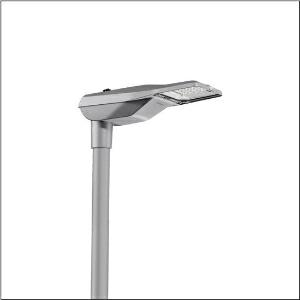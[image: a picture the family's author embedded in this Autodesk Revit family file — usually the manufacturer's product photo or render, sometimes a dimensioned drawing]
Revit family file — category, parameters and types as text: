
# Revit family: streetlight_sl_21_micro___st1_5a_5xe1p43s08db_ce40
name_source: partatom
category: Lighting Fixtures
units: mm (PartAtom-declared; Revit-internal decimal feet)

## family parameters
Cut with Voids When Loaded = No
Host = Face
Light Source = No
Part Type = Normal
Room Calculation Point = No
Round Connector Dimension = Use Diameter
Shared = No

## types (1)
- --- (1 x LED, 5230 lm, 39.1 W, 4000K)
    Apparent Load = 39 VA
    CIE Flux Codes = 22 53 95 100 100
    Color Rendering = 70
    Color Temperature = 4000K
    Default Elevation = 1800 mm
    Description = Streetlight SL 21 micro, mast luminaire, primary light control with lens, of PMMA, primary optical cover: cover, of toughened safety glass, transparent, light distribution: ST1.5a, light emission: direct distribution, primary light characteristic: asymmetric, installation type: side-entry, post-top, LED, High Power LED, rated luminous flux: 5.230lm, luminous efficacy: 134lm/W, light colour: 740, colour temperature: 4000K, control: flexible luminous flux parameterisation, time-dependent luminous flux control, constant luminous flux control, overheat protection, presetting dimming logarithmic, mains connection: 220..240V, AC, 50/60Hz, start of lifetime: 39W, end of service life: 41W, reduction: 18W, luminaire housing, of diecast aluminium, powder-coated, Siteco® metallic grey (DB 702S), corrosivity category C5 mid according to DIN EN ISO 12944, please order mast flange separately, inclination adjustable: 0°, 5°, 10°, 15°, sealing non-destructively replaceable, multi-level sealing system, length: 528mm, width: 235mm, height: 110mm, mast flange for spigot size: 42mm (side-entry): 5XC10008XM4, 60/48mm (side-entry/post-top): 5XC10108XM2, 76/60mm (side-entry/post-top): 5XC10108XM1, Smart Interface above, protection rating (complete): IP66, insulation class (complete): insulation class II (safety insulation), certification: CE, ENEC, ENEC+, VDE, impact resistance: IK09, permissible operating ambient temperature for outdoor applications: -40..+50°C, standard-compliant lighting for roads and squares, packaging unit: 1 piece

Light Distribution: ST1.5a
    Height = 110 mm
    Lamp = 1 x LED
    Lamp Light Flux = 5230 lm
    Lamp Power = 39.1 W
    Lamp count = 1
    Length = 528 mm
    Luminous efficacy = 134 lm/W
    Manufacturer = Siteco
    ModVariant = No
    Model = 5XE1P43S08DB
    Number of Poles = 1
    OnlyDefault = Yes
    Power Factor = 1
    Product Name = Streetlight SL 21 micro | ST1.5a
    Product group = mast luminaire | pylon top
    ProductGroupID = 6100
    Protection Class = Protection class II
    Protection Degree = IP 66
    RLX_Detail_Level = 1
    RLX_Emergency_Light_Flux = 0 lm
    RLX_Emergency_Type = 0
    RLX_Emergency_Type_DB = No
    RlxData = <blob elided: 102337 chars, md5=3875c046>
    Socket = socket
    Standby Power = 0 W
    System Light Flux = 5230 lm
    System Power = 39 W
    Type Comments = factory setting: luminous flux: 100 % | dim-lin: 254 | 765 mA
    Type Image = l_1277292.jpg
    URL = http://relux.com
    VarID = @adj_103867
    Voltage = 0 V
    Weight = 0.00 kg
    Width = 235 mm

## geometry (parser evidence)
native form markers: Blend x4, Sweep x10
no freeform markers — native parametric forms only
